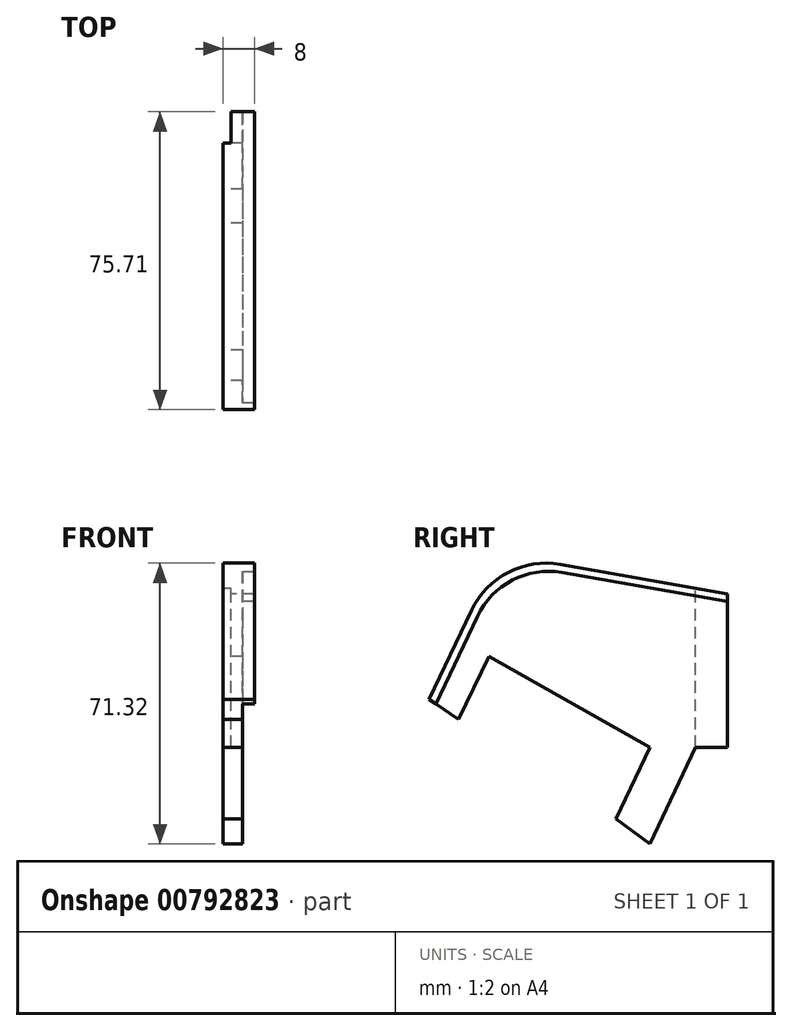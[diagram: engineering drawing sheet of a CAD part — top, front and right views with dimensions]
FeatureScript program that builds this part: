
annotation { "Feature Type Name" : "Feature", "Feature Type Description" : "" }
export const myFeature = defineFeature(function(context is Context, id is Id, definition is map)
    precondition{}
    {
        {
            var Q0;
            Q0=qCreatedBy(makeId("Right.planeOp"),FACE);
            var sketch = newSketch(context, id + "F0", { "sketchPlane" : qUnion([Q0])});
            skLineSegment(sketch, "E0", {"start": v(5.37, -26.5) * mm, "end": v(5.37, 12.5) * mm});
            skLineSegment(sketch, "E1", {"start": v(5.37, 12.5) * mm, "end": v(-52.73, 22.74) * mm});
            skLineSegment(sketch, "E2", {"start": v(-52.73, 22.74) * mm, "end": v(-70.34, -14.4) * mm});
            skLineSegment(sketch, "E3", {"start": v(-14.28, -26.5) * mm, "end": v(-22.92, -44.72) * mm});
            skLineSegment(sketch, "E4", {"start": v(-22.92, -44.72) * mm, "end": v(-14.28, -51.04) * mm});
            skLineSegment(sketch, "E5", {"start": v(-14.28, -51.04) * mm, "end": v(-2.64, -26.5) * mm});
            skLineSegment(sketch, "E6", {"start": v(-2.64, -26.5) * mm, "end": v(5.37, -26.5) * mm});
            skLineSegment(sketch, "E7", {"start": v(-70.34, -14.4) * mm, "end": v(-62.9, -19.46) * mm});
            skLineSegment(sketch, "E8", {"start": v(-14.28, -26.5) * mm, "end": v(-55.16, -3.46) * mm});
            skLineSegment(sketch, "E9", {"start": v(-55.16, -3.46) * mm, "end": v(-62.9, -19.46) * mm});
            skLineSegment(sketch, "E10", {"start": v(-55.16, -3.46) * mm, "end": v(5.37, -16.44) * mm});
            skSolve(sketch);
        }
        {
            var Q0;
            Q0 = qSketchRegion(id + "F0", true);
            extrude(context, id + "F1", {"entities" : qUnion([Q0]), "depth" : 5 * mm, "offsetDistance" : 25 * mm});
        }
        {
            var Q0;
            Q0=makeQuery(id+"F1.opExtrude","CAP_FACE",FACE,{"disambiguationData":[OSD([sQuery(id+"F0.wireOp",EDGE,"E0"),sQuery(id+"F0.wireOp",EDGE,"E1"),sQuery(id+"F0.wireOp",EDGE,"E2"),sQuery(id+"F0.wireOp",EDGE,"snJS27Ut-3CLn-meFN-9GRm-PjXjFzW4VBu6"),sQuery(id+"F0.wireOp",EDGE,"DleCDR5S-FpAI-aNOe-DR92-fq6d2FYKKJof"),sQuery(id+"F0.wireOp",EDGE,"RGl7pVSX-v60Y-Fl4B-fgol-gv0Li8iE5TlU"),sQuery(id+"F0.wireOp",EDGE,"E3"),sQuery(id+"F0.wireOp",EDGE,"E4"),sQuery(id+"F0.wireOp",EDGE,"E5"),sQuery(id+"F0.wireOp",EDGE,"E6")])],"isStart":false});
            var sketch = newSketch(context, id + "F2", { "sketchPlane" : qUnion([Q0])});
            skLineSegment(sketch, "E11", {"start": v(-52.73, 22.74) * mm, "end": v(-52.73, 22.74) * mm});
            skLineSegment(sketch, "E12", {"start": v(-52.73, 22.74) * mm, "end": v(5.37, 12.5) * mm});
            skLineSegment(sketch, "E13", {"start": v(5.37, 12.5) * mm, "end": v(5.37, 10.5) * mm});
            skLineSegment(sketch, "E14", {"start": v(5.37, 10.5) * mm, "end": v(-51.56, 20.54) * mm});
            skLineSegment(sketch, "E15", {"start": v(-70.34, -14.4) * mm, "end": v(-52.73, 22.74) * mm});
            skLineSegment(sketch, "E16", {"start": v(-51.56, 20.54) * mm, "end": v(-68.67, -15.54) * mm});
            skLineSegment(sketch, "E17", {"start": v(-68.67, -15.54) * mm, "end": v(-70.34, -14.4) * mm});
            skSolve(sketch);
        }
        {
            var Q0;
            Q0 = qSketchRegion(id + "F2", true);
            extrude(context, id + "F3", {"entities" : qUnion([Q0]), "operationType" : NewBodyOperationType.ADD, "depth" : 3 * mm, "offsetDistance" : 25 * mm});
        }
        {
            var Q0;
            Q0=makeQuery(id+"F3.opExtrude","SWEPT_EDGE",EDGE,{"disambiguationData":[OSD([sQuery(id+"F2.wireOp",EDGE,"E14"),sQuery(id+"F2.wireOp",EDGE,"PBRFPQbX-8Kfx-tJae-DiEN-10TSIKABqofj")])]});
            fillet(context, id + "F4", {"entities" : qUnion([Q0]), "tangentPropagation" : true, "radius" : 20 * mm, "defaultsChanged" : true, "vertexSettings" : [], "allowEdgeOverflow" : false});
        }
        {
            var Q0;
            Q0=makeQuery(id+"F3.boolean.opBoolean","MERGE",EDGE,{"derivedFrom":[makeQuery(id+"F1.opExtrude","SWEPT_EDGE",EDGE,{"disambiguationData":[OSD([sQuery(id+"F0.wireOp",EDGE,"E1"),sQuery(id+"F0.wireOp",EDGE,"E2")])]}),makeQuery(id+"F3.opExtrude","SWEPT_EDGE",EDGE,{"disambiguationData":[OSD([sQuery(id+"F2.wireOp",EDGE,"E11"),sQuery(id+"F2.wireOp",EDGE,"E12")])]})]});
            fillet(context, id + "F5", {"entities" : qUnion([Q0]), "tangentPropagation" : true, "radius" : 21 * mm, "defaultsChanged" : true, "vertexSettings" : [], "allowEdgeOverflow" : false});
        }
        {
            var Q0;
            Q0=makeQuery(id+"F1.opExtrude","CAP_FACE",FACE,{"disambiguationData":[OSD([sQuery(id+"F0.wireOp",EDGE,"E0"),sQuery(id+"F0.wireOp",EDGE,"E1"),sQuery(id+"F0.wireOp",EDGE,"E2"),sQuery(id+"F0.wireOp",EDGE,"snJS27Ut-3CLn-meFN-9GRm-PjXjFzW4VBu6"),sQuery(id+"F0.wireOp",EDGE,"DleCDR5S-FpAI-aNOe-DR92-fq6d2FYKKJof"),sQuery(id+"F0.wireOp",EDGE,"RGl7pVSX-v60Y-Fl4B-fgol-gv0Li8iE5TlU"),sQuery(id+"F0.wireOp",EDGE,"E3"),sQuery(id+"F0.wireOp",EDGE,"E4"),sQuery(id+"F0.wireOp",EDGE,"E5"),sQuery(id+"F0.wireOp",EDGE,"E6")])],"isStart":true});
            var sketch = newSketch(context, id + "F6", { "sketchPlane" : qUnion([Q0])});
            skLineSegment(sketch, "E18", {"start": v(-5.37, 12.5) * mm, "end": v(-5.37, -26.5) * mm});
            skLineSegment(sketch, "E19", {"start": v(2.64, -26.5) * mm, "end": v(2.64, 13.91) * mm});
            skLineSegment(sketch, "E20", {"start": v(2.64, 13.91) * mm, "end": v(-5.37, 12.5) * mm});
            skLineSegment(sketch, "E21", {"start": v(-5.37, -26.5) * mm, "end": v(2.64, -26.5) * mm});
            skSolve(sketch);
        }
        {
            var Q0;
            Q0 = qSketchRegion(id + "F6", true);
            extrude(context, id + "F7", {"entities" : qUnion([Q0]), "operationType" : NewBodyOperationType.REMOVE, "oppositeDirection" : true, "depth" : 2 * mm, "offsetDistance" : 25 * mm});
        }
    });
